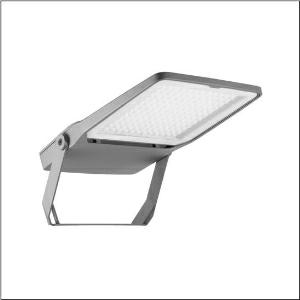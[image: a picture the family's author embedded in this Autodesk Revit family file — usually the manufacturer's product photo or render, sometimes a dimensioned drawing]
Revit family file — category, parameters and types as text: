
# Revit family: floodlight_fl_20_midi___pl43_5xa7682d1a1ac_a646
name_source: partatom
category: Lighting Fixtures
units: mm (PartAtom-declared; Revit-internal decimal feet)

## family parameters
Cut with Voids When Loaded = No
Host = Face
Light Source = No
Part Type = Normal
Room Calculation Point = No
Round Connector Dimension = Use Diameter
Shared = No

## types (1)
- --- (1 x LED 3000K / CRI = 80 (unbekannt), 14980 lm, 3000K)
    Apparent Load = 142 VA
    CIE Flux Codes = 32 74 99 100 100
    Color Rendering = 80
    Color Temperature = 3000K
    Default Elevation = 1800 mm
    Description = Floodlight FL 20 midi, floodlight, primary light control with lens, of plastic, primary optical cover: protective disc, of toughened safety glass, transparent, light distribution: PL43, light emission: direct distribution, primary light characteristic: asymmetric, installation type: surface-mounted, LED, High Power LED, rated luminous flux: 14.980lm, luminous efficacy: 105lm/W, light colour: 830, colour temperature: 3000K, control gear: ECG Plus, control: flexible luminous flux parameterisation, time-dependent luminous flux control, digital communication interface, power reduction, overheat protection, electronic power reduction, with terminal, 5-pole, max. 2.5mm², mains connection: 220..240V, AC, 50/60Hz, rated input power: 142W, LED unit, of diecast aluminium, powder-coated, Siteco® metallic grey (DB 702S), corrosivity category C5 mid according to DIN EN ISO 12944, incl. 1x M20 cable gland for cable Ø 6.5..12mm, length: 654mm, width: 450mm, height: 76mm, housing frame, of diecast aluminium, powder-coated, Siteco® metallic grey (DB 702S), mounting bracket, of steel, powder-coated, Siteco® metallic grey (DB 702S), DALI, protection rating (complete): IP66, insulation class (complete): insulation class II (safety insulation), certification: CE, ENEC, VDE, protection symbol: D, permissible operating ambient temperature: -40..+40°C, permissible operating ambient temperature for outdoor applications: -40..+50°C, standard: DIN EN 12944, packaging unit: 1 piece

Light Distribution: PL43
    Height = 76 mm
    Lamp = 1 x LED 3000K / CRI >= 80 (unbekannt)
    Lamp Light Flux = 14980 lm
    Lamp count = 1
    Length = 672 mm
    Luminous efficacy = 105 lm/W
    Manufacturer = Siteco
    ModVariant = No
    Model = 5XA7682D1A1AC
    Mounting Place = Wall
    Mounting Type = Surface mounted
    Number of Poles = 1
    OnlyDefault = Yes
    Power Factor = 1
    Product Name = Floodlight FL 20 midi | PL43
    Product group = floodlight | wall mounted
    ProductGroupID = 2001
    Protection Class = Protection class II
    Protection Degree = IP 66
    RLX_Detail_Level = 1
    RLX_Emergency_Light_Flux = 0 lm
    RLX_Emergency_Type = 0
    RLX_Emergency_Type_DB = No
    RlxData = <blob elided: 97749 chars, md5=7137d929>
    Socket = socket
    Standby Power = 0 W
    System Light Flux = 14980 lm
    System Power = 142 W
    Type Comments = factory setting: luminous flux: 100 % | dim-lin: 254 | 489 mA
    Type Image = l_1005943.jpg
    URL = http://relux.com
    VarID = @adj_148729
    Voltage = 0 V
    Weight = 0.00 kg
    Width = 450 mm

## geometry (parser evidence)
native form markers: Blend x4, Sweep x12
no freeform markers — native parametric forms only
